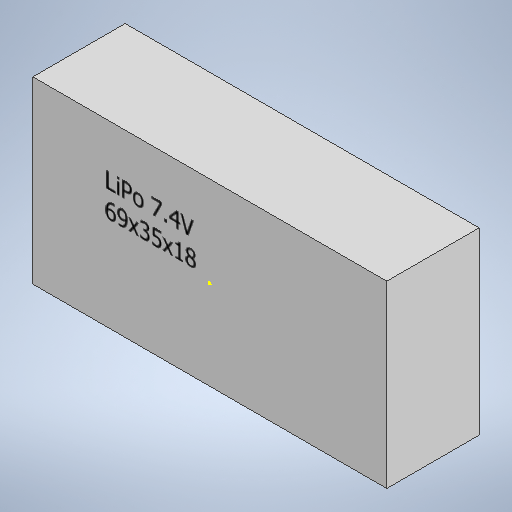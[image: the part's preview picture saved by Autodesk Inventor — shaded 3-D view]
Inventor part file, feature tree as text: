
AUTODESK INVENTOR PART (.ipt)
format: ipt  version: 2025.3 (Build 293356030, 356C)  size: 170,496 bytes
history: native  units: mm
features: sketch x2, other x1, extrude x1
ambient origin geometry x8: Origin, YZ Plane, XZ Plane, XY Plane, X Axis, Y Axis, Z Axis, Center Point
bodies: Body1 (feature_tree)
feature tree (4):
  other  "ソリッド1"
  extrude  "押し出し1"  Depth=69.0mm
  sketch  "スケッチ2"
  sketch  "スケッチ1"
